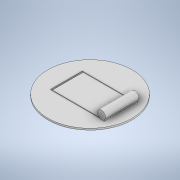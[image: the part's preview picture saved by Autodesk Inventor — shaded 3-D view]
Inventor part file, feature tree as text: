
AUTODESK INVENTOR PART (.ipt)
format: ipt  version: 2021 (Build 250183000, 183)  size: 134,144 bytes
history: native  units: mm
features: extrude x3, sketch x3, other x1
ambient origin geometry x8: Origin, YZ Plane, XZ Plane, XY Plane, X Axis, Y Axis, Z Axis, Center Point
bodies: Body1 (feature_tree)
feature tree (7):
  other  "實體1"
  extrude  "擠出1"  Depth=146.0mm
  extrude  "擠出2"  Depth=2.8mm TaperAngle=0.0deg
  extrude  "擠出3"  Depth=14.0mm
  sketch  "草圖1"
  sketch  "草圖2"
  sketch  "草圖3"
